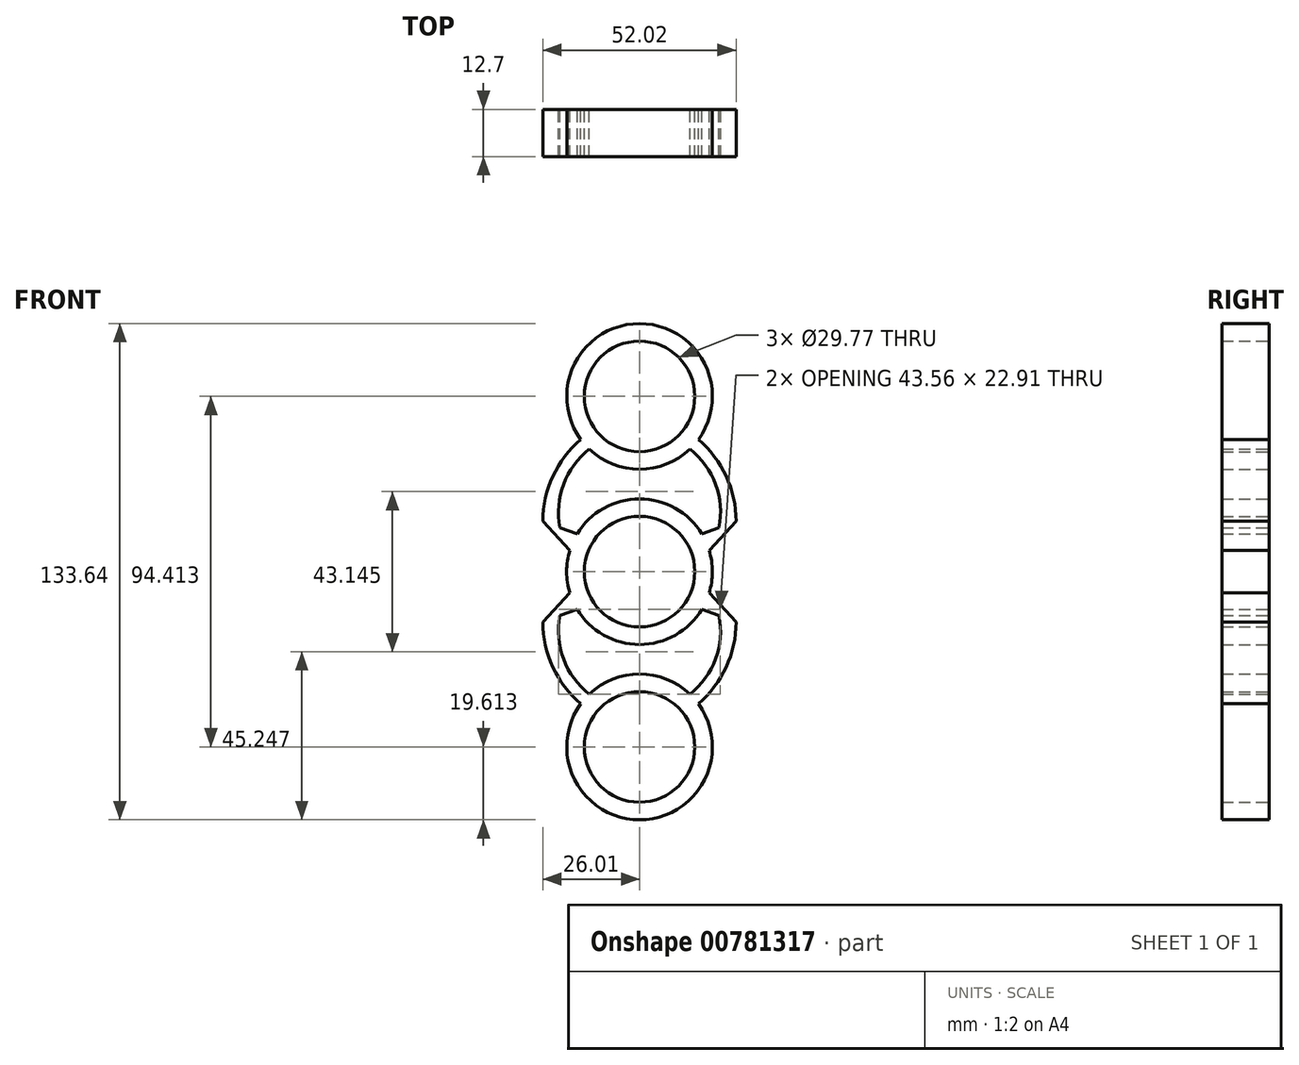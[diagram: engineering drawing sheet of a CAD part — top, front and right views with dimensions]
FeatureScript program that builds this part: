
annotation { "Feature Type Name" : "Feature", "Feature Type Description" : "" }
export const myFeature = defineFeature(function(context is Context, id is Id, definition is map)
    precondition{}
    {
        {
            var Q0;
            Q0=qCreatedBy(makeId("Front.planeOp"),FACE);
            var sketch = newSketch(context, id + "F0", { "sketchPlane" : qUnion([Q0])});
            skCircle(sketch, "E0", {"center": v(0, 0) * mm, "radius": 14.88 * mm});
            skCircle(sketch, "E1", {"center": v(0, 0) * mm, "radius": 19.62 * mm});
            skCircle(sketch, "E2.MirrorC", {"center": v(0.02, -47.2) * mm, "radius": 19.62 * mm});
            skCircle(sketch, "E3.MirrorC", {"center": v(0, -47.2) * mm, "radius": 14.88 * mm});
            skArc(sketch, "E4.MirrorCS", {"start": v(-10.8, -30.84) * mm, "mid": v(-14.2, -22.54) * mm, "end": v(-14.16, -13.57) * mm});
            skArc(sketch, "E5.MirrorCS", {"start": v(10.8, -30.84) * mm, "mid": v(14.2, -22.54) * mm, "end": v(14.16, -13.57) * mm});
            skLineSegment(sketch, "E6", {"start": v(-16.8, -10.12) * mm, "end": v(-26, -13.57) * mm});
            skLineSegment(sketch, "E7", {"start": v(-26, -13.57) * mm, "end": v(-18.75, -5.76) * mm});
            skLineSegment(sketch, "E8.MirrorCS", {"start": v(26, -13.57) * mm, "end": v(18.75, -5.76) * mm});
            skLineSegment(sketch, "E9.MirrorCS", {"start": v(16.8, -10.12) * mm, "end": v(26, -13.57) * mm});
            skArc(sketch, "E10.MirrorCS", {"start": v(0, -24.8) * mm, "mid": v(4.84, -24) * mm, "end": v(9.17, -26.3) * mm});
            skArc(sketch, "E11.MirrorCS", {"start": v(0, -24.8) * mm, "mid": v(-4.84, -24) * mm, "end": v(-9.17, -26.3) * mm});
            skArc(sketch, "E12.MirrorCS", {"start": v(-9.17, -26.3) * mm, "mid": v(0, -21.23) * mm, "end": v(9.17, -26.3) * mm});
            skArc(sketch, "E13", {"start": v(-26, -13.57) * mm, "mid": v(-23.34, -25.71) * mm, "end": v(-15.8, -35.61) * mm});
            skArc(sketch, "E14", {"start": v(-21.4, -11.85) * mm, "mid": v(-20.46, -23.55) * mm, "end": v(-13.54, -33.03) * mm});
            skArc(sketch, "E15.MirrorCS", {"start": v(26, -13.57) * mm, "mid": v(23.34, -25.7) * mm, "end": v(15.82, -35.6) * mm});
            skArc(sketch, "E16.MirrorCS", {"start": v(21.4, -11.85) * mm, "mid": v(20.46, -23.54) * mm, "end": v(13.55, -33.02) * mm});
            skArc(sketch, "E17.MirrorCS", {"start": v(10.8, 30.84) * mm, "mid": v(14.2, 22.54) * mm, "end": v(14.16, 13.57) * mm});
            skLineSegment(sketch, "E18.MirrorCS", {"start": v(16.8, 10.12) * mm, "end": v(26, 13.57) * mm});
            skLineSegment(sketch, "E19.MirrorCS", {"start": v(26, 13.57) * mm, "end": v(18.75, 5.76) * mm});
            skArc(sketch, "E20.MirrorCS", {"start": v(21.4, 11.85) * mm, "mid": v(20.46, 23.54) * mm, "end": v(13.55, 33.02) * mm});
            skArc(sketch, "E21.MirrorCS", {"start": v(26, 13.57) * mm, "mid": v(23.34, 25.7) * mm, "end": v(15.82, 35.6) * mm});
            skArc(sketch, "E22.MirrorCS", {"start": v(-9.17, 26.3) * mm, "mid": v(0, 21.23) * mm, "end": v(9.17, 26.3) * mm});
            skArc(sketch, "E23.MirrorCS", {"start": v(0, 24.8) * mm, "mid": v(4.84, 24) * mm, "end": v(9.17, 26.3) * mm});
            skArc(sketch, "E24.MirrorCS", {"start": v(0, 24.8) * mm, "mid": v(-4.84, 24) * mm, "end": v(-9.17, 26.3) * mm});
            skArc(sketch, "E25.MirrorCS", {"start": v(-10.8, 30.84) * mm, "mid": v(-14.2, 22.54) * mm, "end": v(-14.16, 13.57) * mm});
            skArc(sketch, "E26.MirrorCS", {"start": v(-21.4, 11.85) * mm, "mid": v(-20.46, 23.55) * mm, "end": v(-13.54, 33.03) * mm});
            skArc(sketch, "E27.MirrorCS", {"start": v(-26, 13.57) * mm, "mid": v(-23.34, 25.71) * mm, "end": v(-15.8, 35.61) * mm});
            skLineSegment(sketch, "E28.MirrorCS", {"start": v(-16.8, 10.12) * mm, "end": v(-26, 13.57) * mm});
            skLineSegment(sketch, "E29.MirrorCS", {"start": v(-26, 13.57) * mm, "end": v(-18.75, 5.76) * mm});
            skCircle(sketch, "E30.MirrorC", {"center": v(0.02, 47.2) * mm, "radius": 19.62 * mm});
            skCircle(sketch, "E31.MirrorC", {"center": v(0, 47.2) * mm, "radius": 14.88 * mm});
            skSolve(sketch);
        }
        {
            var Q0;
            Q0 = qSketchRegion(id + "F0", true);
            extrude(context, id + "F1", {"entities" : qUnion([Q0]), "depth" : 12.7 * mm, "offsetDistance" : 25.4 * mm});
        }
    });
